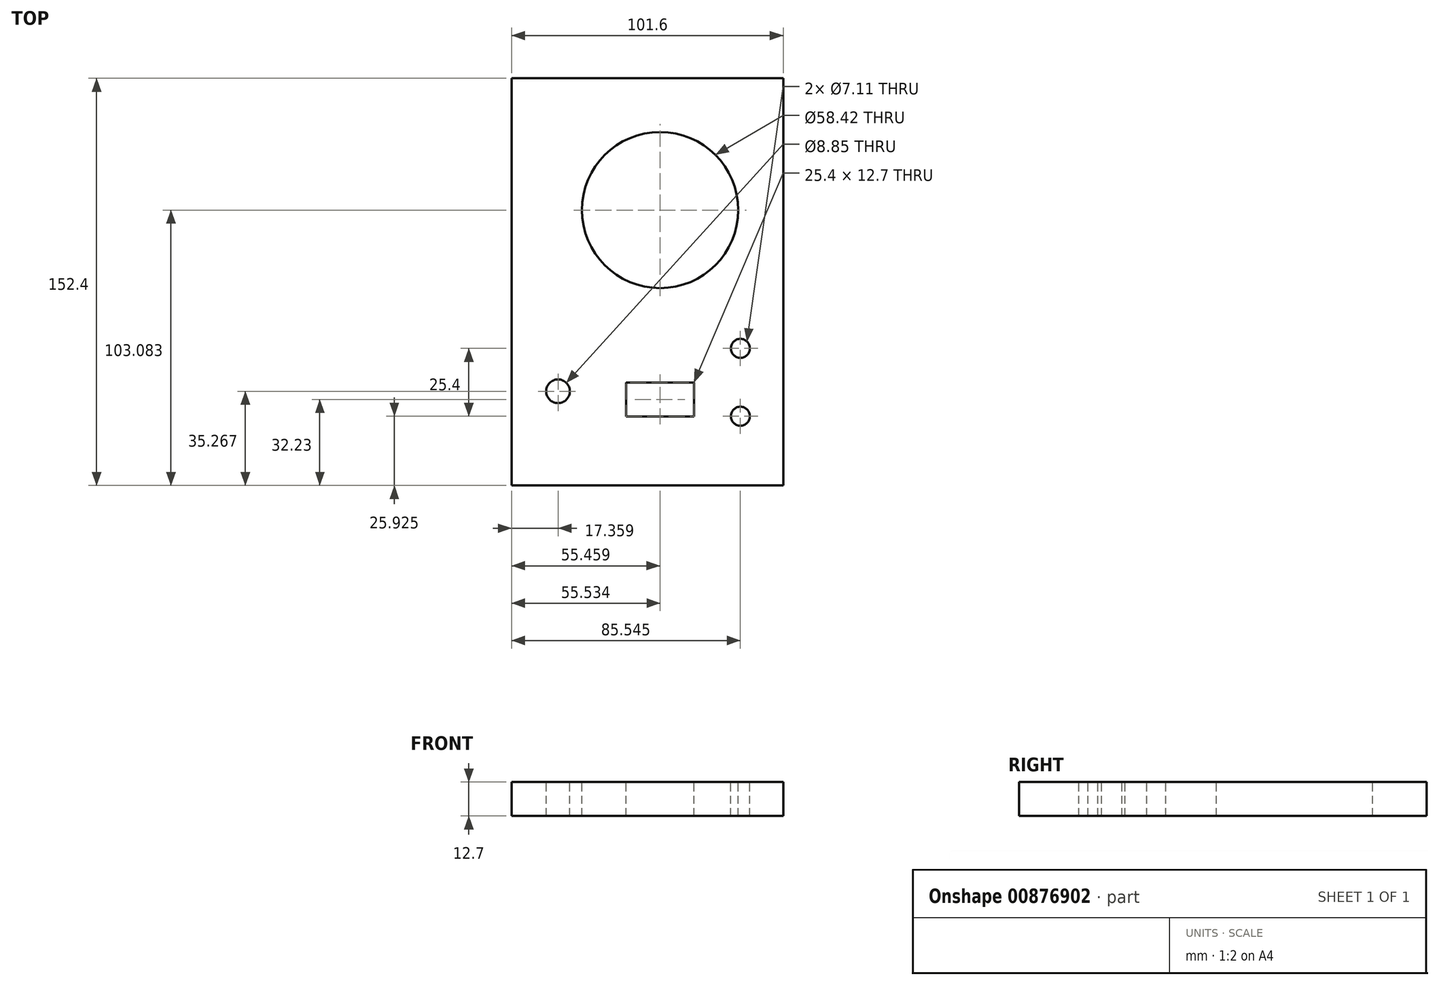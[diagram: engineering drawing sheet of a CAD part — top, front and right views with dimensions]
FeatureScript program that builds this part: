
annotation { "Feature Type Name" : "Feature", "Feature Type Description" : "" }
export const myFeature = defineFeature(function(context is Context, id is Id, definition is map)
    precondition{}
    {
        {
            var Q0;
            Q0=qCreatedBy(makeId("Top.planeOp"),FACE);
            var sketch = newSketch(context, id + "F0", { "sketchPlane" : qUnion([Q0])});
            skLineSegment(sketch, "E0.bottom", {"start": v(-137.35, 90.58) * mm, "end": v(-35.75, 90.58) * mm});
            skLineSegment(sketch, "E0.top", {"start": v(-137.35, -61.82) * mm, "end": v(-35.75, -61.82) * mm});
            skLineSegment(sketch, "E0.left", {"start": v(-137.35, 90.58) * mm, "end": v(-137.35, -61.82) * mm});
            skLineSegment(sketch, "E0.right", {"start": v(-35.75, 90.58) * mm, "end": v(-35.75, -61.82) * mm});
            skSolve(sketch);
        }
        {
            var Q0;
            Q0=qCreatedBy(makeId("Top.planeOp"),FACE);
            var sketch = newSketch(context, id + "F1", { "sketchPlane" : qUnion([Q0])});
            skCircle(sketch, "E1", {"center": v(-81.82, 41.26) * mm, "radius": 29.21 * mm});
            skSolve(sketch);
        }
        {
            var Q0;
            Q0=qCreatedBy(makeId("Top.planeOp"),FACE);
            var sketch = newSketch(context, id + "F2", { "sketchPlane" : qUnion([Q0])});
            skCircle(sketch, "E2", {"center": v(-120, -26.55) * mm, "radius": 4.43 * mm});
            skLineSegment(sketch, "E3.bottom", {"start": v(-94.6, -23.24) * mm, "end": v(-69.2, -23.24) * mm});
            skLineSegment(sketch, "E3.top", {"start": v(-94.6, -35.94) * mm, "end": v(-69.2, -35.94) * mm});
            skLineSegment(sketch, "E3.left", {"start": v(-94.6, -23.24) * mm, "end": v(-94.6, -35.94) * mm});
            skLineSegment(sketch, "E3.right", {"start": v(-69.2, -23.24) * mm, "end": v(-69.2, -35.94) * mm});
            skSolve(sketch);
        }
        {
            var Q0;
            Q0=qCreatedBy(makeId("Top.planeOp"),FACE);
            var sketch = newSketch(context, id + "F3", { "sketchPlane" : qUnion([Q0])});
            skCircle(sketch, "E4", {"center": v(-51.8, -10.5) * mm, "radius": 3.56 * mm});
            skCircle(sketch, "E5", {"center": v(-51.8, -35.9) * mm, "radius": 3.56 * mm});
            skSolve(sketch);
        }
        {
            var Q0;
            Q0=makeQuery(id+"F0.imprint","IMPRINT",FACE,{"disambiguationData":[TD([[makeQuery(id+"F0.imprint","IMPRINT",EDGE,{"derivedFrom":sQuery(id+"F0.wireOp",EDGE,"E0.bottom")}),-1.0]])]});
            extrude(context, id + "F4", {"entities" : qUnion([Q0]), "depth" : 12.7 * mm, "offsetDistance" : 25.4 * mm});
        }
        {
            var Q0;
            Q0=makeQuery(id+"F1.imprint","IMPRINT",FACE,{"disambiguationData":[TD([[makeQuery(id+"F1.imprint","IMPRINT",EDGE,{"derivedFrom":sQuery(id+"F1.wireOp",EDGE,"E1")}),1.0]])]});
            var Q1;
            Q1=makeQuery(id+"F2.imprint","IMPRINT",FACE,{"disambiguationData":[TD([[makeQuery(id+"F2.imprint","IMPRINT",EDGE,{"derivedFrom":sQuery(id+"F2.wireOp",EDGE,"E2")}),1.0]])]});
            var Q2;
            Q2=makeQuery(id+"F2.imprint","IMPRINT",FACE,{"disambiguationData":[TD([[makeQuery(id+"F2.imprint","IMPRINT",EDGE,{"derivedFrom":sQuery(id+"F2.wireOp",EDGE,"E3.bottom")}),-1.0]])]});
            var Q3;
            Q3=makeQuery(id+"F3.imprint","IMPRINT",FACE,{"disambiguationData":[TD([[makeQuery(id+"F3.imprint","IMPRINT",EDGE,{"derivedFrom":sQuery(id+"F3.wireOp",EDGE,"E4")}),1.0]])]});
            var Q4;
            Q4=makeQuery(id+"F3.imprint","IMPRINT",FACE,{"disambiguationData":[TD([[makeQuery(id+"F3.imprint","IMPRINT",EDGE,{"derivedFrom":sQuery(id+"F3.wireOp",EDGE,"E5")}),1.0]])]});
            extrude(context, id + "F5", {"entities" : qUnion([Q0, Q1, Q2, Q3, Q4]), "operationType" : NewBodyOperationType.ADD, "depth" : 25.4 * mm, "offsetDistance" : 25.4 * mm});
        }
        {
            var Q0;
            Q0=makeQuery(id+"F5.opExtrude","CAP_FACE",FACE,{"disambiguationData":[OSD([sQuery(id+"F2.wireOp",EDGE,"E3.bottom"),sQuery(id+"F2.wireOp",EDGE,"E3.top"),sQuery(id+"F2.wireOp",EDGE,"E3.left"),sQuery(id+"F2.wireOp",EDGE,"E3.right")])],"isStart":false});
            var Q1;
            Q1=makeQuery(id+"F5.opExtrude","CAP_FACE",FACE,{"disambiguationData":[OSD([sQuery(id+"F1.wireOp",EDGE,"E1")])],"isStart":false});
            var Q2;
            Q2=makeQuery(id+"F5.opExtrude","CAP_FACE",FACE,{"disambiguationData":[OSD([sQuery(id+"F3.wireOp",EDGE,"E4")])],"isStart":false});
            var Q3;
            Q3=makeQuery(id+"F5.opExtrude","CAP_FACE",FACE,{"disambiguationData":[OSD([sQuery(id+"F3.wireOp",EDGE,"E5")])],"isStart":false});
            var Q4;
            Q4=makeQuery(id+"F5.opExtrude","CAP_FACE",FACE,{"disambiguationData":[OSD([sQuery(id+"F2.wireOp",EDGE,"E2")])],"isStart":false});
            extrude(context, id + "F6", {"entities" : qUnion([Q0, Q1, Q2, Q3, Q4]), "operationType" : NewBodyOperationType.REMOVE, "oppositeDirection" : true, "depth" : 25.4 * mm, "offsetDistance" : 25.4 * mm});
        }
    });
